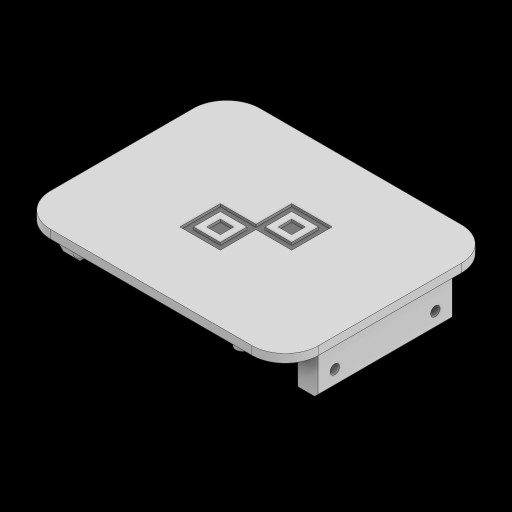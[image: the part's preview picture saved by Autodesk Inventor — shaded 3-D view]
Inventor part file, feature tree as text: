
AUTODESK INVENTOR PART (.ipt)
format: ipt  version: 2024 (Build 280153000, 153)  size: 235,008 bytes
history: native  units: mm
features: sketch x5, extrude x4, fillet x1, hole x1, chamfer x1, projected_geometry x1
ambient origin geometry x8: Origin, YZ Plane, XZ Plane, XY Plane, X Axis, Y Axis, Z Axis, Center Point
bodies: Volumenkörper1 (feature_tree)
feature tree (13):
  extrude  "Extrusion1"  Depth=125.0mm
  fillet  "Rundung1"  Radius=5.0mm
  extrude  "Extrusion2"  Depth=21.333333mm
  extrude  "Extrusion3"  Depth=21.333333mm
  extrude  "Extrusion4"  Depth=1.5mm TaperAngle=0.0deg
  hole  "Bohrung1"  [1 undecoded]
  chamfer  "Fasen1"  Distance=30.0mm
  sketch  "Skizze1"  dims[d0=160.0mm d1=125.0mm d2=5.0mm d3=0.0mm]
  sketch  "Skizze2"  dims[d4=20.0mm]
  sketch  "Skizze3"  dims[d14=8.0mm d15=8.0mm d16=16.0mm d17=16.0mm d18=24.0mm d20=21.333333mm]
  sketch  "Skizze4"  dims[d21=21.333333mm d22=62.5mm]
  sketch  "Skizze5"  dims[d23=80.0mm d24=8.0mm d25=8.0mm d26=16.0mm d27=16.0mm d28=24.0mm d29=1.5mm d30=0.0mm d31=9.0mm d32=30.0mm d33=8.0mm d34=78.5mm d35=95.5mm d36=8.0mm d37=8.0mm d38=8.0mm d39=4.0mm d40=4.0mm d41=4.0mm d42=4.0mm d43=7.0mm d44=0.0mm d45=3.0mm d46=80.0mm d47=40.0mm d48=12.0mm d49=3.0mm d50=12.0mm d51=80.0mm d52=40.0mm d53=25.0mm d54=0.0mm d55=30.0mm d56=30.0mm d57=15.0mm d58=15.0mm d59=5.6mm d60=6.0mm d61=9.4mm d62=2.0mm d63=90.0deg d64=8.0mm d65=20.594885mm d66=2.0mm d67=2.0mm d68=45.0deg]
  projected_geometry  "Projizierte Kontur1"
note: 1 required parameter value undecoded (feature->parameter linkage not recoverable at this tier; creation-order binding heuristic only, values carry confidence <= 0.55)
